# Revit family: WicStyle65Evo - 1 Leaf Inward Opening
name_source: partatom
category: Doors
revit_build: Autodesk Revit Architecture 2014 (Build: 20130308_1515(x64)
units: mm (PartAtom-declared; Revit-internal decimal feet)

## types (2) — shared parameters
Analytic Construction = <None>
Date of publishing = 3/14/2015
Design country = Germany
Edition number = 1
Frame 1916002 = No
Frame 1916003 = No
Frame 1926500 = No
Frame 1926501 = No
Frame Depth = 65 mm  [stored 0.213255 ft]
Frame Projection Ext. = 25 mm  [stored 0.082021 ft]
Frame Projection Int. = 25 mm  [stored 0.082021 ft]
FrameWarning = 1
Function = Interior
Glass Elevation = 9 mm  [stored 0.0295276 ft]
Glass Offset Bottom = 129 mm
Glass Thickness = 24 mm  [stored 0.0787402 ft]
Glass offset side/top = 113 mm  [stored 0.370735 ft]
GlassLayer Thickness In = 5 mm  [stored 0.0164042 ft]
GlassLayer Thickness Out = 5 mm  [stored 0.0164042 ft]
Handle Height = 850 mm  [stored 2.78871 ft]
Handle Material = Aluminium
Handle Offset X = 30 mm  [stored 0.0984252 ft]
Height = 2100 mm
Manufacturer = Wicona
Manufacturer country = Germany
Manufacturer name = Wicona
Material main = Aluminium
Material secondary = Glass
Nominal height = 210000
Nominal width = 150000
Product Guid = 1ef816c7-8b64-491b-b226-0f81c5fb437c
Product SKU = WICSTYLE_65_EVO_D
Product data url = http://bimobject.com
Product family = Windows & Doors
Product group = Windows
QR code = http://bimobject.com
Rough Height = 1034 mm  [stored 3.39239 ft]
Sash 1926510 = Yes
Sash 1926511 = No
Sash 1926512 = No
Sash 1926535 = No
Sash Bottom 1926517 = No
SashBottomWarning = 1
SashWarning = 1
Threshold 1926524 = No
Threshold 1926525 = No
Threshold 3021033 = No
Threshold 3926500 = No
ThresholdWarning = 1
URL = http://www.wicona.com
Wall Closure = By host
WarningSign = No
Width = 900 mm  [stored 2.95276 ft]
zero-valued in all types: Weight Net (Kg)

## per-type parameters (varying)
- F-1926502 / S-192610 / B-1926516 / Th-3926502: Frame 1916004=No; Frame 1926502=Yes; Frame Material=Aluminium; Frame Width=78 mm  [stored 0.255906 ft]; Frame Width 1=71 mm  [stored 0.23294 ft]; Frame Width 2=56 mm  [stored 0.183727 ft]; Frame Width 3=46 mm  [stored 0.150919 ft]; Glass Material=<By Category>; Leaf Height=2003 mm  [stored 6.57152 ft]; Leaf Material=Aluminium; Leaf Width=744 mm  [stored 2.44094 ft]; Opening Line Length=808 mm; Sash Bottom 1926516=Yes; Sash Bottom 1926518=No; Threshold 1926526=No; Threshold 3926502=Yes; Threshold Height=21 mm  [stored 0.0688976 ft]; Threshold Length=808 mm
- F-1916004 / S-1926512 / B-1926518 / Th-3926526: Acoustic=RA,tr = 35 dB; Air Permeability=Class 4; Corrosion Resistance of the Fittings=NPD; Description=Wicslide 65 sliding windows and patio doors is the perfect solution for combining high thermal performance and large sizes. With  its  various  designs  of  outer  and  opening  frames, multiple  leaf  combinations  (from  2  to  6  leaves)  and  its  comprehensive range of dual colour solutions, the Wicslide 65 brings greater freedom to building design. Designed  to  meet  market  demands,  Wicslide  65  sliding doors are perfectly suited for disabled access.; EN1627 Burglar Resistance=NPD; Frame 1916004=Yes; Frame 1926502=No; Frame Material=WICONA - Aluminium - RAL7016 - Anthracite Grey - Matt; Frame Width=72 mm  [stored 0.23622 ft]; Frame Width 1=65 mm  [stored 0.213255 ft]; Frame Width 2=50 mm  [stored 0.164042 ft]; Frame Width 3=40 mm  [stored 0.131234 ft]; Glass Material=WICONA -  Glass; Keynote=L10/330; Leaf Height=2009 mm; Leaf Material=WICONA - Aluminium - RAL7016 - Anthracite Grey - Matt; Leaf Width=756 mm  [stored 2.48031 ft]; Load Bearing Capacity of Safety Devices=Fulfilled; Maximum Sash Weight=150kg as standard design, heavier weights can easily be customised; Mechanical Strength=Class 4; Model=Wicslide 65 evo; Opening Line Length=820 mm; Operating Forces=Class 1; Operation=IFC_DOORDBLSWING; Quality Assurance=Certified according to ISO 9001:2008; Repeated Opening/Closing=Class 2 (10,000 Cycles); Sash Bottom 1926516=No; Sash Bottom 1926518=Yes; Threshold 1926526=Yes; Threshold 3926502=No; Threshold Height=31 mm  [stored 0.101706 ft]; Threshold Length=820 mm; Uniclass2=Ss-25-30-95-28; Watertightness=E900

note: [stored X ft] marks values corroborated as IEEE doubles in the binary element streams (Revit-internal decimal feet)

## geometry (parser evidence)
native form markers: Blend x4, Sweep x22
no freeform markers — native parametric forms only
